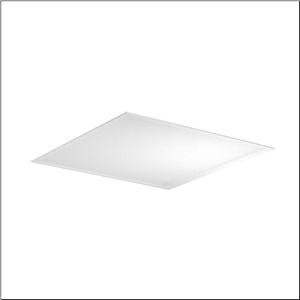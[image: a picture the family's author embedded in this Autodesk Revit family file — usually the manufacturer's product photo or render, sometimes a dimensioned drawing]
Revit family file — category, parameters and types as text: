
# Revit family: apollon_r__21_square_51mq12wd2m14_c270
name_source: partatom
category: Lighting Fixtures
units: mm (PartAtom-declared; Revit-internal decimal feet)

## family parameters
Cut with Voids When Loaded = No
Host = Face
Light Source = No
Part Type = Normal
Room Calculation Point = No
Round Connector Dimension = Use Diameter
Shared = No

## types (1)
- --- (1 x LED, 4200 lm, 26 W, 4000K)
    Apparent Load = 26 VA
    CIE Flux Codes = 60 87 97 100 100
    Color Rendering = 80
    Color Temperature = 4000K
    Default Elevation = 1800 mm
    Description = Apollon® 21 square, office luminaire, primary optical cover: micro prismatic cover, of PMMA, CAT 2 (L<= 3000cd/m²), light emission: direct distribution, primary light characteristic: symmetric, installation type: lay-in mounting, LED, rated luminous flux: 4.200lm, luminous efficacy: 162lm/W, light colour: 830/840, colour temperature: 3000/4000K, with terminal, 5-pole, mains connection: 220..240V, AC/DC, 0/50..60Hz, rated input power: 26W, housing, of aluminium, coated, traffic white (RAL 9016), module: M600, length: 595mm, width: 595mm, height: 30mm, housing upper side, of sheet steel, galvanised, protection rating (complete): IP20, protection rating (lamp compartment, on room side): IP50, insulation class (complete): insulation class II (safety insulation), certification: CE, ENEC, impact resistance: IK03, permissible operating ambient temperature: -20..+45°C, permissible storage temperature: -40..+80°C, packaging unit: 1 piece
    Height = 0 mm  [stored 0 ft]
    Lamp = 1 x LED
    Lamp Light Flux = 4200 lm
    Lamp Power = 26 W
    Lamp count = 1
    Length = 595 mm
    Luminous efficacy = 162 lm/W
    Manufacturer = Siteco
    ModVariant = No
    Model = 51MQ12WD2M14
    Mounting Place = Ceiling
    Mounting Type = Recessed
    Number of Poles = 1
    OnlyDefault = Yes
    Power Factor = 1
    Product Name = Apollon® 21 square
    Product group = office luminaire | ceiling recessed
    ProductGroupID = 400
    Protection Class = Protection class II
    Protection Degree = IP 20
    RLX_Detail_Level = 1
    RLX_Emergency_Light_Flux = 0 lm
    RLX_Emergency_Type = 0
    RLX_Emergency_Type_DB = No
    RlxData = <blob elided: 12681 chars, md5=e8f4c48f>
    Socket = socket
    Standby Power = 0 W
    System Light Flux = 4200 lm
    System Power = 26 W
    Type Comments = factory setting
    Type Image = l_1291049.jpg
    URL = http://relux.com
    VarID = @adj_036387
    Voltage = 0 V
    Weight = 0.00 kg
    Width = 595 mm

note: [stored X ft] marks values corroborated as IEEE doubles in the binary element streams (Revit-internal decimal feet)

## geometry (parser evidence)
native form markers: Sweep x12
no freeform markers — native parametric forms only
